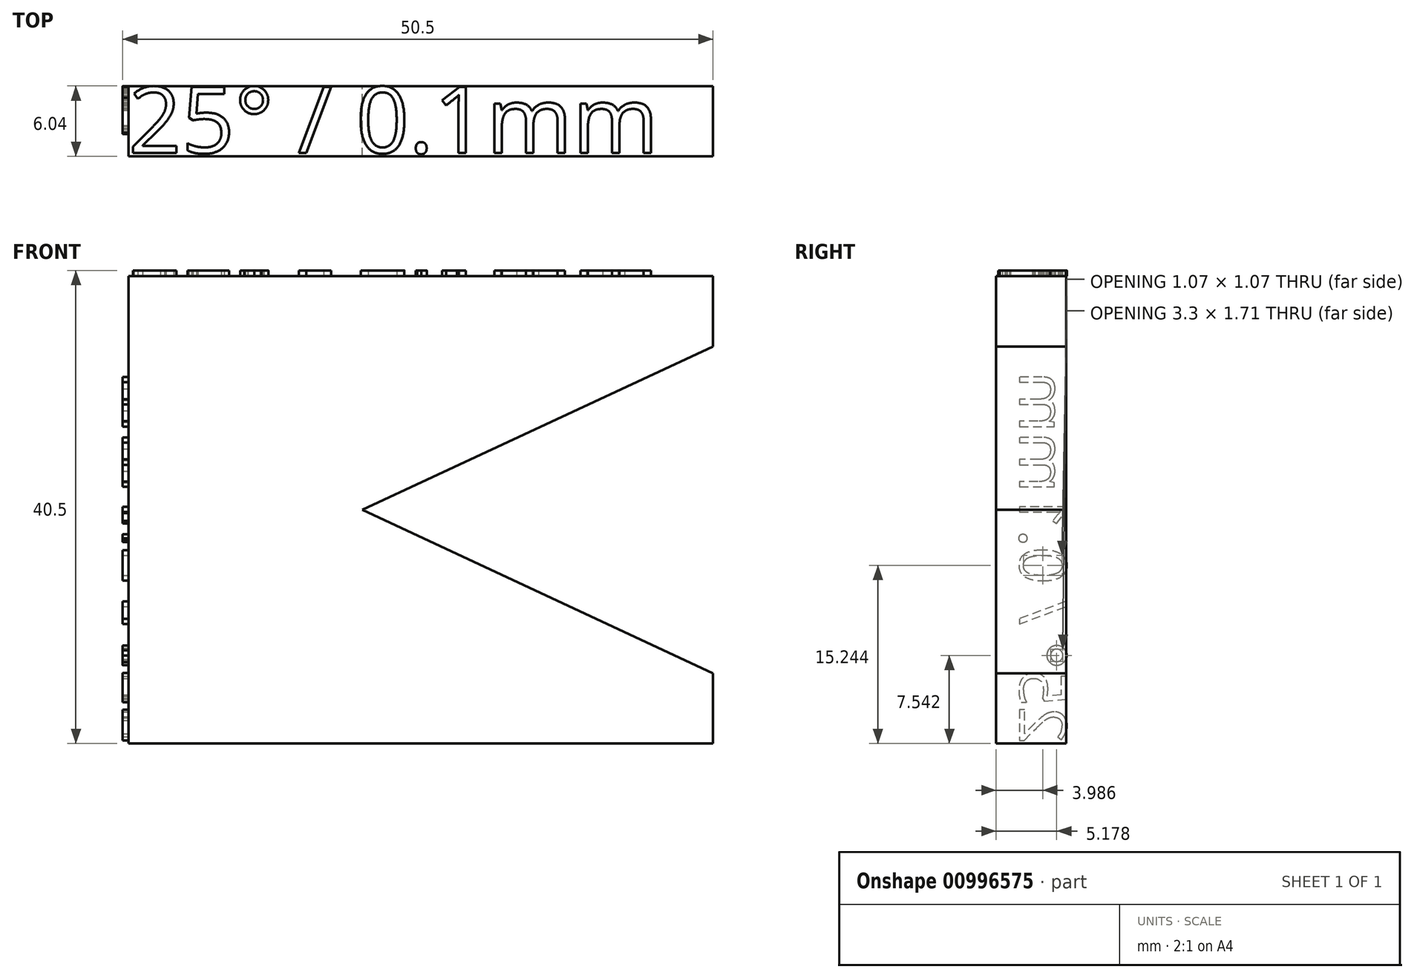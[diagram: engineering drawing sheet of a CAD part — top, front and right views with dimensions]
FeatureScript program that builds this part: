
annotation { "Feature Type Name" : "Feature", "Feature Type Description" : "" }
export const myFeature = defineFeature(function(context is Context, id is Id, definition is map)
    precondition{}
    {
        {
            var Q0;
            Q0=qCreatedBy(makeId("Front.planeOp"),FACE);
            var sketch = newSketch(context, id + "F0", { "sketchPlane" : qUnion([Q0])});
            skLineSegment(sketch, "E0", {"start": v(0, 39.45) * mm, "end": v(0, -35.1) * mm, "construction": true});
            skLineSegment(sketch, "E1", {"start": v(-35.77, 0) * mm, "end": v(35.97, 0) * mm, "construction": true});
            skLineSegment(sketch, "E2", {"start": v(-20, 20) * mm, "end": v(-20, -20) * mm});
            skLineSegment(sketch, "E3", {"start": v(-20, -20) * mm, "end": v(30, -20) * mm});
            skLineSegment(sketch, "E4", {"start": v(0, 0) * mm, "end": v(30, -13.99) * mm});
            skLineSegment(sketch, "E5", {"start": v(30, -13.99) * mm, "end": v(30, -20) * mm});
            skLineSegment(sketch, "E6.MirrorCS", {"start": v(0, 0) * mm, "end": v(30, 13.99) * mm});
            skLineSegment(sketch, "E7.MirrorCS", {"start": v(30, 13.99) * mm, "end": v(30, 20) * mm});
            skLineSegment(sketch, "E8.MirrorCS", {"start": v(-20, 20) * mm, "end": v(30, 20) * mm});
            skSolve(sketch);
        }
        {
            var Q0;
            Q0=makeQuery(id+"F0.imprint","IMPRINT",FACE,{"disambiguationData":[TD([[makeQuery(id+"F0.imprint","IMPRINT",EDGE,{"derivedFrom":sQuery(id+"F0.wireOp",EDGE,"E2")}),1.0]])]});
            extrude(context, id + "F1", {"entities" : qUnion([Q0]), "depth" : 6 * mm, "offsetDistance" : 25 * mm});
        }
        {
            var Q0;
            Q0=makeQuery(id+"F1.opExtrude","SWEPT_FACE",FACE,{"disambiguationData":[OSD([sQuery(id+"F0.wireOp",EDGE,"E8.MirrorCS")])]});
            var sketch = newSketch(context, id + "F2", { "sketchPlane" : qUnion([Q0])});
            skText(sketch, "E9", { "text": "25° / 0.1mm", "fontName": "OpenSans-Regular.ttf"});
            const initialGuessF2  = {"E9": [-0.02, -0.0057, 1, 0, 0.0057]};
            skSetInitialGuess(sketch, initialGuessF2);
            skSolve(sketch);
        }
        {
            var Q0;
            Q0 = qSketchRegion(id + "F2", true);
            extrude(context, id + "F3", {"entities" : qUnion([Q0]), "operationType" : NewBodyOperationType.ADD, "depth" : 0.5 * mm, "offsetDistance" : 25 * mm});
        }
        {
            var Q0;
            Q0=makeQuery(id+"F1.opExtrude","SWEPT_FACE",FACE,{"disambiguationData":[OSD([sQuery(id+"F0.wireOp",EDGE,"E2")])]});
            var sketch = newSketch(context, id + "F4", { "sketchPlane" : qUnion([Q0])});
            skText(sketch, "E10", { "text": "25° / 0.1mm", "fontName": "OpenSans-Regular.ttf"});
            const initialGuessF4  = {"E10": [0, -0.024, 1, 0, 0.004]};
            skSetInitialGuess(sketch, initialGuessF4);
            skSolve(sketch);
        }
        {
            var Q0;
            Q0 = qSketchRegion(id + "F4", true);
            extrude(context, id + "F5", {"entities" : qUnion([Q0]), "depth" : 0.5 * mm, "offsetDistance" : 25 * mm});
        }
        {
            var Q0;
            Q0=makeQuery(id+"F5.opExtrude","SWEPT_BODY",BODY,{"disambiguationData":[OSD([sQuery(id+"F4.wireOp",EDGE,"E10.sketch_text.stroke-0"),sQuery(id+"F4.wireOp",EDGE,"E10.sketch_text.stroke-1"),sQuery(id+"F4.wireOp",EDGE,"E10.sketch_text.stroke-2"),sQuery(id+"F4.wireOp",EDGE,"E10.sketch_text.stroke-3"),sQuery(id+"F4.wireOp",EDGE,"E10.sketch_text.stroke-4"),sQuery(id+"F4.wireOp",EDGE,"E10.sketch_text.stroke-5"),sQuery(id+"F4.wireOp",EDGE,"E10.sketch_text.stroke-6"),sQuery(id+"F4.wireOp",EDGE,"E10.sketch_text.stroke-7"),sQuery(id+"F4.wireOp",EDGE,"E10.sketch_text.stroke-8"),sQuery(id+"F4.wireOp",EDGE,"E10.sketch_text.stroke-9"),sQuery(id+"F4.wireOp",EDGE,"E10.sketch_text.stroke-10"),sQuery(id+"F4.wireOp",EDGE,"E10.sketch_text.stroke-11"),sQuery(id+"F4.wireOp",EDGE,"E10.sketch_text.stroke-12"),sQuery(id+"F4.wireOp",EDGE,"E10.sketch_text.stroke-13"),sQuery(id+"F4.wireOp",EDGE,"E10.sketch_text.stroke-14"),sQuery(id+"F4.wireOp",EDGE,"E10.sketch_text.stroke-15"),sQuery(id+"F4.wireOp",EDGE,"E10.sketch_text.stroke-16"),sQuery(id+"F4.wireOp",EDGE,"E10.sketch_text.stroke-17"),sQuery(id+"F4.wireOp",EDGE,"E10.sketch_text.stroke-18"),sQuery(id+"F4.wireOp",EDGE,"E10.sketch_text.stroke-19")])]});
            var Q1;
            Q1=makeQuery(id+"F5.opExtrude","SWEPT_BODY",BODY,{"disambiguationData":[OSD([sQuery(id+"F4.wireOp",EDGE,"E10.sketch_text.stroke-20"),sQuery(id+"F4.wireOp",EDGE,"E10.sketch_text.stroke-21"),sQuery(id+"F4.wireOp",EDGE,"E10.sketch_text.stroke-22"),sQuery(id+"F4.wireOp",EDGE,"E10.sketch_text.stroke-23"),sQuery(id+"F4.wireOp",EDGE,"E10.sketch_text.stroke-24"),sQuery(id+"F4.wireOp",EDGE,"E10.sketch_text.stroke-25"),sQuery(id+"F4.wireOp",EDGE,"E10.sketch_text.stroke-26"),sQuery(id+"F4.wireOp",EDGE,"E10.sketch_text.stroke-27"),sQuery(id+"F4.wireOp",EDGE,"E10.sketch_text.stroke-28"),sQuery(id+"F4.wireOp",EDGE,"E10.sketch_text.stroke-29"),sQuery(id+"F4.wireOp",EDGE,"E10.sketch_text.stroke-30"),sQuery(id+"F4.wireOp",EDGE,"E10.sketch_text.stroke-31"),sQuery(id+"F4.wireOp",EDGE,"E10.sketch_text.stroke-32"),sQuery(id+"F4.wireOp",EDGE,"E10.sketch_text.stroke-33"),sQuery(id+"F4.wireOp",EDGE,"E10.sketch_text.stroke-34"),sQuery(id+"F4.wireOp",EDGE,"E10.sketch_text.stroke-35"),sQuery(id+"F4.wireOp",EDGE,"E10.sketch_text.stroke-36"),sQuery(id+"F4.wireOp",EDGE,"E10.sketch_text.stroke-37"),sQuery(id+"F4.wireOp",EDGE,"E10.sketch_text.stroke-38")])]});
            var Q2;
            Q2=makeQuery(id+"F5.opExtrude","SWEPT_BODY",BODY,{"disambiguationData":[OSD([sQuery(id+"F4.wireOp",EDGE,"E10.sketch_text.stroke-39"),sQuery(id+"F4.wireOp",EDGE,"E10.sketch_text.stroke-40"),sQuery(id+"F4.wireOp",EDGE,"E10.sketch_text.stroke-41"),sQuery(id+"F4.wireOp",EDGE,"E10.sketch_text.stroke-42"),sQuery(id+"F4.wireOp",EDGE,"E10.sketch_text.stroke-43"),sQuery(id+"F4.wireOp",EDGE,"E10.sketch_text.stroke-44"),sQuery(id+"F4.wireOp",EDGE,"E10.sketch_text.stroke-45"),sQuery(id+"F4.wireOp",EDGE,"E10.sketch_text.stroke-46"),sQuery(id+"F4.wireOp",EDGE,"E10.sketch_text.stroke-47"),sQuery(id+"F4.wireOp",EDGE,"E10.sketch_text.stroke-48"),sQuery(id+"F4.wireOp",EDGE,"E10.sketch_text.stroke-49"),sQuery(id+"F4.wireOp",EDGE,"E10.sketch_text.stroke-50"),sQuery(id+"F4.wireOp",EDGE,"E10.sketch_text.stroke-51"),sQuery(id+"F4.wireOp",EDGE,"E10.sketch_text.stroke-52"),sQuery(id+"F4.wireOp",EDGE,"E10.sketch_text.stroke-53"),sQuery(id+"F4.wireOp",EDGE,"E10.sketch_text.stroke-54"),sQuery(id+"F4.wireOp",EDGE,"E10.sketch_text.stroke-55")])]});
            var Q3;
            Q3=makeQuery(id+"F5.opExtrude","SWEPT_BODY",BODY,{"disambiguationData":[OSD([sQuery(id+"F4.wireOp",EDGE,"E10.sketch_text.stroke-56"),sQuery(id+"F4.wireOp",EDGE,"E10.sketch_text.stroke-57"),sQuery(id+"F4.wireOp",EDGE,"E10.sketch_text.stroke-58"),sQuery(id+"F4.wireOp",EDGE,"E10.sketch_text.stroke-59")])]});
            var Q4;
            Q4=makeQuery(id+"F5.opExtrude","SWEPT_BODY",BODY,{"disambiguationData":[OSD([sQuery(id+"F4.wireOp",EDGE,"E10.sketch_text.stroke-60"),sQuery(id+"F4.wireOp",EDGE,"E10.sketch_text.stroke-61"),sQuery(id+"F4.wireOp",EDGE,"E10.sketch_text.stroke-62"),sQuery(id+"F4.wireOp",EDGE,"E10.sketch_text.stroke-63"),sQuery(id+"F4.wireOp",EDGE,"E10.sketch_text.stroke-64"),sQuery(id+"F4.wireOp",EDGE,"E10.sketch_text.stroke-65"),sQuery(id+"F4.wireOp",EDGE,"E10.sketch_text.stroke-66"),sQuery(id+"F4.wireOp",EDGE,"E10.sketch_text.stroke-67"),sQuery(id+"F4.wireOp",EDGE,"E10.sketch_text.stroke-68"),sQuery(id+"F4.wireOp",EDGE,"E10.sketch_text.stroke-69"),sQuery(id+"F4.wireOp",EDGE,"E10.sketch_text.stroke-70"),sQuery(id+"F4.wireOp",EDGE,"E10.sketch_text.stroke-71"),sQuery(id+"F4.wireOp",EDGE,"E10.sketch_text.stroke-72"),sQuery(id+"F4.wireOp",EDGE,"E10.sketch_text.stroke-73"),sQuery(id+"F4.wireOp",EDGE,"E10.sketch_text.stroke-74"),sQuery(id+"F4.wireOp",EDGE,"E10.sketch_text.stroke-75")])]});
            var Q5;
            Q5=makeQuery(id+"F5.opExtrude","SWEPT_BODY",BODY,{"disambiguationData":[OSD([sQuery(id+"F4.wireOp",EDGE,"E10.sketch_text.stroke-76"),sQuery(id+"F4.wireOp",EDGE,"E10.sketch_text.stroke-77"),sQuery(id+"F4.wireOp",EDGE,"E10.sketch_text.stroke-78"),sQuery(id+"F4.wireOp",EDGE,"E10.sketch_text.stroke-79"),sQuery(id+"F4.wireOp",EDGE,"E10.sketch_text.stroke-80"),sQuery(id+"F4.wireOp",EDGE,"E10.sketch_text.stroke-81"),sQuery(id+"F4.wireOp",EDGE,"E10.sketch_text.stroke-82"),sQuery(id+"F4.wireOp",EDGE,"E10.sketch_text.stroke-83")])]});
            var Q6;
            Q6=makeQuery(id+"F5.opExtrude","SWEPT_BODY",BODY,{"disambiguationData":[OSD([sQuery(id+"F4.wireOp",EDGE,"E10.sketch_text.stroke-84"),sQuery(id+"F4.wireOp",EDGE,"E10.sketch_text.stroke-85"),sQuery(id+"F4.wireOp",EDGE,"E10.sketch_text.stroke-86"),sQuery(id+"F4.wireOp",EDGE,"E10.sketch_text.stroke-87"),sQuery(id+"F4.wireOp",EDGE,"E10.sketch_text.stroke-88"),sQuery(id+"F4.wireOp",EDGE,"E10.sketch_text.stroke-89"),sQuery(id+"F4.wireOp",EDGE,"E10.sketch_text.stroke-90"),sQuery(id+"F4.wireOp",EDGE,"E10.sketch_text.stroke-91"),sQuery(id+"F4.wireOp",EDGE,"E10.sketch_text.stroke-92")])]});
            var Q7;
            Q7=makeQuery(id+"F5.opExtrude","SWEPT_BODY",BODY,{"disambiguationData":[OSD([sQuery(id+"F4.wireOp",EDGE,"E10.sketch_text.stroke-93"),sQuery(id+"F4.wireOp",EDGE,"E10.sketch_text.stroke-94"),sQuery(id+"F4.wireOp",EDGE,"E10.sketch_text.stroke-95"),sQuery(id+"F4.wireOp",EDGE,"E10.sketch_text.stroke-96"),sQuery(id+"F4.wireOp",EDGE,"E10.sketch_text.stroke-97"),sQuery(id+"F4.wireOp",EDGE,"E10.sketch_text.stroke-98"),sQuery(id+"F4.wireOp",EDGE,"E10.sketch_text.stroke-99"),sQuery(id+"F4.wireOp",EDGE,"E10.sketch_text.stroke-100"),sQuery(id+"F4.wireOp",EDGE,"E10.sketch_text.stroke-101"),sQuery(id+"F4.wireOp",EDGE,"E10.sketch_text.stroke-102"),sQuery(id+"F4.wireOp",EDGE,"E10.sketch_text.stroke-103"),sQuery(id+"F4.wireOp",EDGE,"E10.sketch_text.stroke-104"),sQuery(id+"F4.wireOp",EDGE,"E10.sketch_text.stroke-105"),sQuery(id+"F4.wireOp",EDGE,"E10.sketch_text.stroke-106"),sQuery(id+"F4.wireOp",EDGE,"E10.sketch_text.stroke-107"),sQuery(id+"F4.wireOp",EDGE,"E10.sketch_text.stroke-108"),sQuery(id+"F4.wireOp",EDGE,"E10.sketch_text.stroke-109"),sQuery(id+"F4.wireOp",EDGE,"E10.sketch_text.stroke-110"),sQuery(id+"F4.wireOp",EDGE,"E10.sketch_text.stroke-111"),sQuery(id+"F4.wireOp",EDGE,"E10.sketch_text.stroke-112"),sQuery(id+"F4.wireOp",EDGE,"E10.sketch_text.stroke-113"),sQuery(id+"F4.wireOp",EDGE,"E10.sketch_text.stroke-114"),sQuery(id+"F4.wireOp",EDGE,"E10.sketch_text.stroke-115"),sQuery(id+"F4.wireOp",EDGE,"E10.sketch_text.stroke-116"),sQuery(id+"F4.wireOp",EDGE,"E10.sketch_text.stroke-117"),sQuery(id+"F4.wireOp",EDGE,"E10.sketch_text.stroke-118"),sQuery(id+"F4.wireOp",EDGE,"E10.sketch_text.stroke-119"),sQuery(id+"F4.wireOp",EDGE,"E10.sketch_text.stroke-120")])]});
            var Q8;
            Q8=makeQuery(id+"F5.opExtrude","SWEPT_BODY",BODY,{"disambiguationData":[OSD([sQuery(id+"F4.wireOp",EDGE,"E10.sketch_text.stroke-121"),sQuery(id+"F4.wireOp",EDGE,"E10.sketch_text.stroke-122"),sQuery(id+"F4.wireOp",EDGE,"E10.sketch_text.stroke-123"),sQuery(id+"F4.wireOp",EDGE,"E10.sketch_text.stroke-124"),sQuery(id+"F4.wireOp",EDGE,"E10.sketch_text.stroke-125"),sQuery(id+"F4.wireOp",EDGE,"E10.sketch_text.stroke-126"),sQuery(id+"F4.wireOp",EDGE,"E10.sketch_text.stroke-127"),sQuery(id+"F4.wireOp",EDGE,"E10.sketch_text.stroke-128"),sQuery(id+"F4.wireOp",EDGE,"E10.sketch_text.stroke-129"),sQuery(id+"F4.wireOp",EDGE,"E10.sketch_text.stroke-130"),sQuery(id+"F4.wireOp",EDGE,"E10.sketch_text.stroke-131"),sQuery(id+"F4.wireOp",EDGE,"E10.sketch_text.stroke-132"),sQuery(id+"F4.wireOp",EDGE,"E10.sketch_text.stroke-133"),sQuery(id+"F4.wireOp",EDGE,"E10.sketch_text.stroke-134"),sQuery(id+"F4.wireOp",EDGE,"E10.sketch_text.stroke-135"),sQuery(id+"F4.wireOp",EDGE,"E10.sketch_text.stroke-136"),sQuery(id+"F4.wireOp",EDGE,"E10.sketch_text.stroke-137"),sQuery(id+"F4.wireOp",EDGE,"E10.sketch_text.stroke-138"),sQuery(id+"F4.wireOp",EDGE,"E10.sketch_text.stroke-139"),sQuery(id+"F4.wireOp",EDGE,"E10.sketch_text.stroke-140"),sQuery(id+"F4.wireOp",EDGE,"E10.sketch_text.stroke-141"),sQuery(id+"F4.wireOp",EDGE,"E10.sketch_text.stroke-142"),sQuery(id+"F4.wireOp",EDGE,"E10.sketch_text.stroke-143"),sQuery(id+"F4.wireOp",EDGE,"E10.sketch_text.stroke-144"),sQuery(id+"F4.wireOp",EDGE,"E10.sketch_text.stroke-145"),sQuery(id+"F4.wireOp",EDGE,"E10.sketch_text.stroke-146"),sQuery(id+"F4.wireOp",EDGE,"E10.sketch_text.stroke-147"),sQuery(id+"F4.wireOp",EDGE,"E10.sketch_text.stroke-148")])]});
            var Q9;
            Q9=makeQuery(id+"F1.opExtrude","CAP_EDGE",EDGE,{"disambiguationData":[OSD([sQuery(id+"F0.wireOp",EDGE,"E3")])],"isStart":true});
            transform(context, id + "F6", {"entities" : qUnion([Q0, Q1, Q2, Q3, Q4, Q5, Q6, Q7, Q8]), "transformType" : TransformType.ROTATION, "transformAxis" : qUnion([Q9]), "angle" : 90 * degree, "oppositeDirection" : true, "makeCopy" : false});
        }
    });
